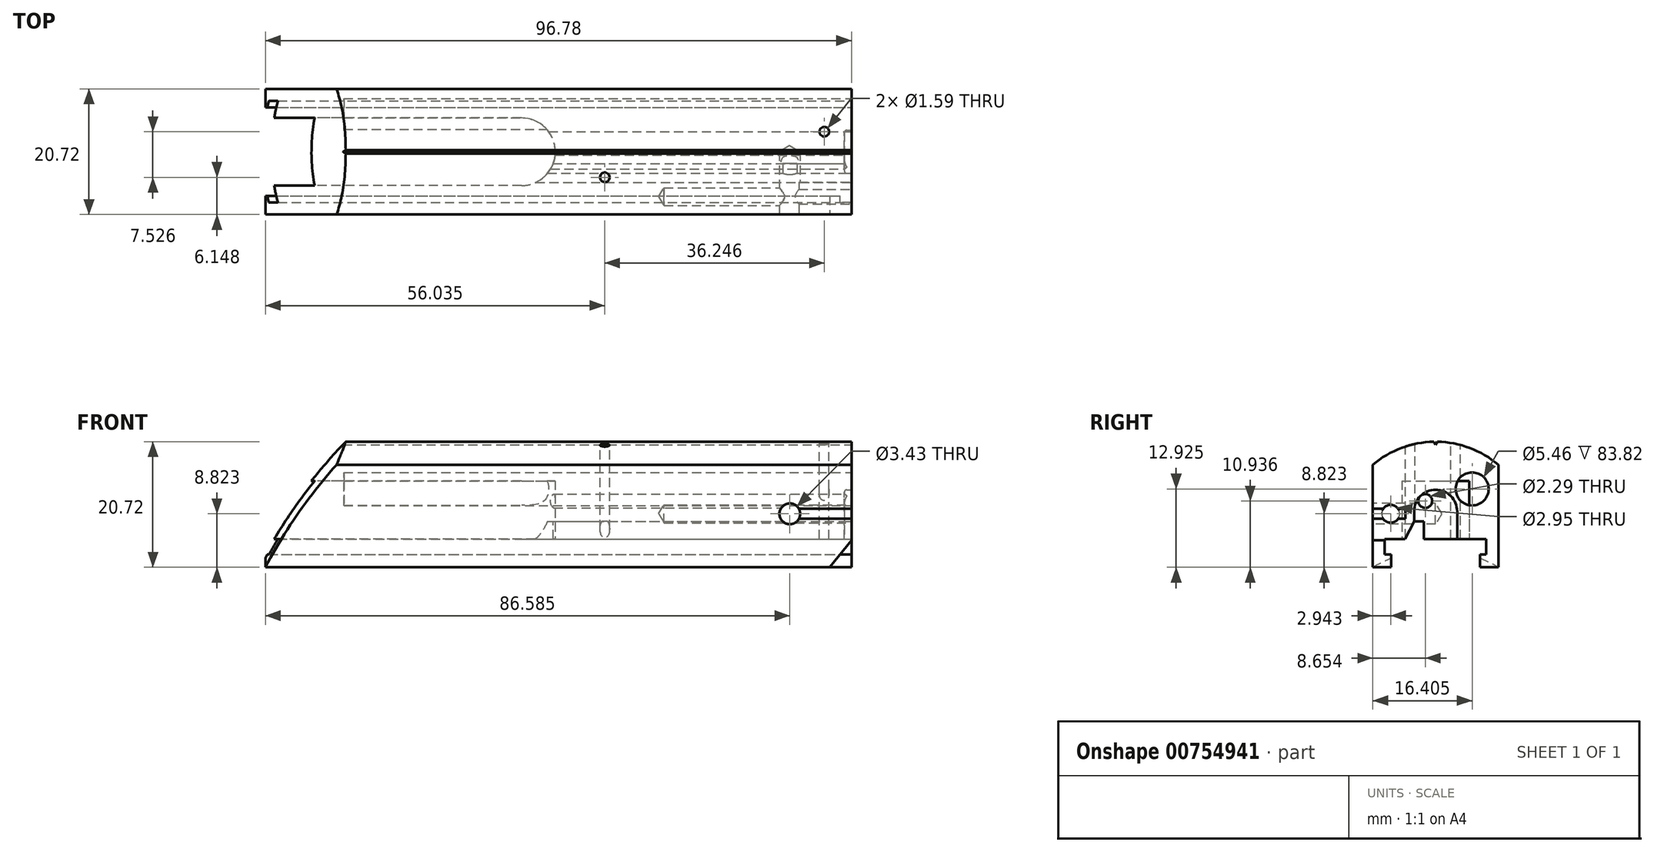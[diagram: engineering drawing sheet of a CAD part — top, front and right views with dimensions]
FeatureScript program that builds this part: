
annotation { "Feature Type Name" : "Feature", "Feature Type Description" : "" }
export const myFeature = defineFeature(function(context is Context, id is Id, definition is map)
    precondition{}
    {
        {
            var Q0;
            Q0=qCreatedBy(makeId("Right.planeOp"),FACE);
            var sketch = newSketch(context, id + "F0", { "sketchPlane" : qUnion([Q0])});
            skLineSegment(sketch, "E0.bottom", {"start": v(-10.36, -10.36) * mm, "end": v(10.36, -10.36) * mm});
            skLineSegment(sketch, "E0.top", {"start": v(-10.36, 10.36) * mm, "end": v(10.36, 10.36) * mm});
            skLineSegment(sketch, "E0.left", {"start": v(-10.36, -10.36) * mm, "end": v(-10.36, 10.36) * mm});
            skLineSegment(sketch, "E0.right", {"start": v(10.36, -10.36) * mm, "end": v(10.36, 10.36) * mm});
            skPoint(sketch, "E0.middle", {"position": v(0, 0) * mm});
            skSolve(sketch);
        }
        {
            var Q0;
            Q0 = qSketchRegion(id + "F0", true);
            var Q1;
            Q1=makeQuery(id+"F0.imprint","IMPRINT",FACE,{"disambiguationData":[TD([[makeQuery(id+"F0.imprint","IMPRINT",EDGE,{"derivedFrom":sQuery(id+"F0.wireOp",EDGE,"E0.bottom")}),1.0]])]});
            extrude(context, id + "F1", {"entities" : qUnion([Q0, Q1]), "endBound" : BoundingType.SYMMETRIC, "depth" : 96.77 * mm, "offsetDistance" : 25.4 * mm});
        }
        {
            var Q0;
            Q0=makeQuery(id+"F1.opExtrude","CAP_FACE",FACE,{"disambiguationData":[OSD([sQuery(id+"F0.wireOp",EDGE,"E0.bottom"),sQuery(id+"F0.wireOp",EDGE,"E0.top"),sQuery(id+"F0.wireOp",EDGE,"E0.left"),sQuery(id+"F0.wireOp",EDGE,"E0.right")])],"isStart":true});
            var sketch = newSketch(context, id + "F2", { "sketchPlane" : qUnion([Q0])});
            skLineSegment(sketch, "E1.bottom", {"start": v(5.58, 3.91) * mm, "end": v(-5.58, 3.91) * mm});
            skLineSegment(sketch, "E1.top", {"start": v(5.58, -10.36) * mm, "end": v(-5.58, -10.36) * mm});
            skLineSegment(sketch, "E1.left", {"start": v(5.58, 3.91) * mm, "end": v(5.58, -10.36) * mm});
            skLineSegment(sketch, "E1.right", {"start": v(-5.58, 3.91) * mm, "end": v(-5.58, -10.36) * mm});
            skSolve(sketch);
        }
        {
            var Q0;
            Q0=makeQuery(id+"F2.imprint","IMPRINT",FACE,{"disambiguationData":[TD([[makeQuery(id+"F2.imprint","IMPRINT",EDGE,{"derivedFrom":sQuery(id+"F2.wireOp",EDGE,"E1.bottom")}),1.0]])]});
            extrude(context, id + "F3", {"entities" : qUnion([Q0]), "operationType" : NewBodyOperationType.REMOVE, "oppositeDirection" : true, "depth" : 47.85 * mm, "offsetDistance" : 25.4 * mm});
        }
        {
            var Q0;
            Q0=makeQuery(id+"F3.boolean.opBoolean","COPY",EDGE,{"derivedFrom":makeQuery(id+"F3.opExtrude","CAP_EDGE",EDGE,{"disambiguationData":[OSD([sQuery(id+"F2.wireOp",EDGE,"E1.right")])],"isStart":false})});
            var Q1;
            Q1=makeQuery(id+"F3.boolean.opBoolean","COPY",EDGE,{"derivedFrom":makeQuery(id+"F3.opExtrude","CAP_EDGE",EDGE,{"disambiguationData":[OSD([sQuery(id+"F2.wireOp",EDGE,"E1.left")])],"isStart":false})});
            fillet(context, id + "F4", {"entities" : qUnion([Q0, Q1]), "radius" : 5.56 * mm, "tangentPropagation" : true, "allowEdgeOverflow" : false});
        }
        {
            var Q0;
            Q0=makeQuery(id+"F1.opExtrude","CAP_FACE",FACE,{"disambiguationData":[OSD([sQuery(id+"F0.wireOp",EDGE,"E0.bottom"),sQuery(id+"F0.wireOp",EDGE,"E0.top"),sQuery(id+"F0.wireOp",EDGE,"E0.left"),sQuery(id+"F0.wireOp",EDGE,"E0.right")])],"isStart":false});
            var sketch = newSketch(context, id + "F5", { "sketchPlane" : qUnion([Q0])});
            skLineSegment(sketch, "E2.bottom", {"start": v(-8.38, -5.7) * mm, "end": v(8.38, -5.7) * mm});
            skLineSegment(sketch, "E2.top", {"start": v(-8.38, -8.26) * mm, "end": v(-7.32, -8.26) * mm});
            skLineSegment(sketch, "E2.left", {"start": v(-8.38, -5.7) * mm, "end": v(-8.38, -8.25) * mm});
            skLineSegment(sketch, "E2.right", {"start": v(8.38, -5.7) * mm, "end": v(8.38, -8.25) * mm});
            skLineSegment(sketch, "E3.top", {"start": v(-7.32, -10.36) * mm, "end": v(7.32, -10.36) * mm});
            skLineSegment(sketch, "E3.left", {"start": v(-7.32, -8.25) * mm, "end": v(-7.32, -10.36) * mm});
            skLineSegment(sketch, "E3.right", {"start": v(7.32, -8.25) * mm, "end": v(7.32, -10.36) * mm});
            skLineSegment(sketch, "E4.trimOffspring", {"start": v(7.32, -8.26) * mm, "end": v(8.38, -8.26) * mm});
            skPoint(sketch, "E5", {"position": v(0, -5.7) * mm});
            skSolve(sketch);
        }
        {
            var Q0;
            Q0=makeQuery(id+"F5.imprint","IMPRINT",FACE,{"disambiguationData":[TD([[makeQuery(id+"F5.imprint","IMPRINT",EDGE,{"derivedFrom":sQuery(id+"F5.wireOp",EDGE,"E2.bottom")}),-1.0]])]});
            extrude(context, id + "F6", {"entities" : qUnion([Q0]), "operationType" : NewBodyOperationType.REMOVE, "endBound" : BoundingType.THROUGH_ALL, "oppositeDirection" : true, "depth" : 25.4 * mm, "offsetDistance" : 25.4 * mm});
        }
        {
            var Q0;
            Q0=makeQuery(id+"F1.opExtrude","CAP_FACE",FACE,{"disambiguationData":[OSD([sQuery(id+"F0.wireOp",EDGE,"E0.bottom"),sQuery(id+"F0.wireOp",EDGE,"E0.top"),sQuery(id+"F0.wireOp",EDGE,"E0.left"),sQuery(id+"F0.wireOp",EDGE,"E0.right")])],"isStart":false});
            var sketch = newSketch(context, id + "F7", { "sketchPlane" : qUnion([Q0])});
            skLineSegment(sketch, "E6.bottom", {"start": v(-1.97, -5.7) * mm, "end": v(-5.08, -5.7) * mm});
            skLineSegment(sketch, "E6.top", {"start": v(-1.97, -2.78) * mm, "end": v(-3.56, -2.78) * mm});
            skLineSegment(sketch, "E6.left", {"start": v(-1.97, -5.7) * mm, "end": v(-1.97, -2.78) * mm});
            skLineSegment(sketch, "E7", {"start": v(-5.08, -5.7) * mm, "end": v(-3.56, -2.78) * mm});
            skPoint(sketch, "E6.right.end.orphan", {"position": v(-5.14, -2.78) * mm});
            skSolve(sketch);
        }
        {
            var Q0;
            Q0=makeQuery(id+"F7.imprint","IMPRINT",FACE,{"disambiguationData":[TD([[makeQuery(id+"F7.imprint","IMPRINT",EDGE,{"derivedFrom":sQuery(id+"F7.wireOp",EDGE,"E6.bottom")}),1.0]])]});
            extrude(context, id + "F8", {"entities" : qUnion([Q0]), "operationType" : NewBodyOperationType.REMOVE, "endBound" : BoundingType.THROUGH_ALL, "oppositeDirection" : true, "depth" : 25.4 * mm, "offsetDistance" : 25.4 * mm});
        }
        {
            var Q0;
            Q0=makeQuery(id+"F1.opExtrude","CAP_FACE",FACE,{"disambiguationData":[OSD([sQuery(id+"F0.wireOp",EDGE,"E0.bottom"),sQuery(id+"F0.wireOp",EDGE,"E0.top"),sQuery(id+"F0.wireOp",EDGE,"E0.left"),sQuery(id+"F0.wireOp",EDGE,"E0.right")])],"isStart":false});
            var sketch = newSketch(context, id + "F9", { "sketchPlane" : qUnion([Q0])});
            skArc(sketch, "E8", {"start": v(3.56, -1.13) * mm, "mid": v(0, 2.43) * mm, "end": v(-3.56, -1.13) * mm});
            skLineSegment(sketch, "E9.top", {"start": v(-3.56, -5.7) * mm, "end": v(3.56, -5.7) * mm});
            skLineSegment(sketch, "E9.left", {"start": v(-3.56, -1.07) * mm, "end": v(-3.56, -5.7) * mm});
            skLineSegment(sketch, "E9.right", {"start": v(3.56, -1.07) * mm, "end": v(3.56, -5.7) * mm});
            skSolve(sketch);
        }
        {
            var Q0;
            {var subQ1=sQuery(id+"F9.wireOp",EDGE,"E8");Q0=makeQuery(id+"F9.imprint","IMPRINT",FACE,{"disambiguationData":[TD([[makeQuery(id+"F9.imprint","IMPRINT",EDGE,{"derivedFrom":subQ1}),1.0]])]});}
            extrude(context, id + "F10", {"entities" : qUnion([Q0]), "operationType" : NewBodyOperationType.REMOVE, "oppositeDirection" : true, "depth" : 1.17 * mm, "offsetDistance" : 25.4 * mm});
        }
        {
            var Q0;
            Q0=makeQuery(id+"F10.boolean.opBoolean","COPY",EDGE,{"derivedFrom":makeQuery(id+"F10.opExtrude","CAP_EDGE",EDGE,{"disambiguationData":[OSD([sQuery(id+"F9.wireOp",EDGE,"E9.right")])],"isStart":false})});
            var Q1;
            Q1=makeQuery(id+"F10.boolean.opBoolean","COPY",EDGE,{"derivedFrom":makeQuery(id+"F10.opExtrude","CAP_EDGE",EDGE,{"disambiguationData":[OSD([sQuery(id+"F9.wireOp",EDGE,"E8")])],"isStart":false})});
            var Q2;
            Q2=makeQuery(id+"F10.boolean.opBoolean","COPY",EDGE,{"derivedFrom":makeQuery(id+"F10.opExtrude","CAP_EDGE",EDGE,{"disambiguationData":[OSD([sQuery(id+"F9.wireOp",EDGE,"E9.left")])],"isStart":false})});
            fillet(context, id + "F11", {"entities" : qUnion([Q0, Q1, Q2]), "radius" : 0.38 * mm, "tangentPropagation" : true, "allowEdgeOverflow" : false});
        }
        {
            var Q0;
            Q0=makeQuery(id+"F1.opExtrude","CAP_FACE",FACE,{"disambiguationData":[OSD([sQuery(id+"F0.wireOp",EDGE,"E0.bottom"),sQuery(id+"F0.wireOp",EDGE,"E0.top"),sQuery(id+"F0.wireOp",EDGE,"E0.left"),sQuery(id+"F0.wireOp",EDGE,"E0.right")])],"isStart":false});
            var sketch = newSketch(context, id + "F12", { "sketchPlane" : qUnion([Q0])});
            skLineSegment(sketch, "E10", {"start": v(-2.51, 1.38) * mm, "end": v(0, -1.13) * mm, "construction": true});
            skPoint(sketch, "E11", {"position": v(-1.7, 0.58) * mm});
            skSolve(sketch);
        }
        {
            var Q0;
            Q0=sQuery(id+"F12.wireOp",VERTEX,"E11");
            var Q1;
            Q1=makeQuery(id+"F1.opExtrude","SWEPT_BODY",BODY,{"disambiguationData":[OSD([sQuery(id+"F0.wireOp",EDGE,"E0.bottom"),sQuery(id+"F0.wireOp",EDGE,"E0.top"),sQuery(id+"F0.wireOp",EDGE,"E0.left"),sQuery(id+"F0.wireOp",EDGE,"E0.right")])]});
            hole(context, id + "F13", {"style" : HoleStyle.SIMPLE, "endStyle" : HoleEndStyle.THROUGH, "holeDiameter" : 2.3 * mm, "majorDiameter" : 6.35 * mm, "isTappedThrough" : true, "tappedDepth" : 18.41 * mm, "tapClearance" : 3, "startFromSketch" : true, "locations" : qUnion([Q0]), "scope" : qUnion([Q1])});
        }
        {
            var Q0;
            Q0=makeQuery(id+"F1.opExtrude","SWEPT_FACE",FACE,{"disambiguationData":[OSD([sQuery(id+"F0.wireOp",EDGE,"E0.left")])]});
            var sketch = newSketch(context, id + "F14", { "sketchPlane" : qUnion([Q0])});
            skPoint(sketch, "E12", {"position": v(38.2, -1.54) * mm});
            skSolve(sketch);
        }
        {
            var Q0;
            Q0=sQuery(id+"F14.wireOp",VERTEX,"E12");
            var Q1;
            Q1=makeQuery(id+"F1.opExtrude","SWEPT_BODY",BODY,{"disambiguationData":[OSD([sQuery(id+"F0.wireOp",EDGE,"E0.bottom"),sQuery(id+"F0.wireOp",EDGE,"E0.top"),sQuery(id+"F0.wireOp",EDGE,"E0.left"),sQuery(id+"F0.wireOp",EDGE,"E0.right")])]});
            hole(context, id + "F15", {"style" : HoleStyle.SIMPLE, "endStyle" : HoleEndStyle.BLIND, "holeDiameter" : 3.43 * mm, "majorDiameter" : 6.35 * mm, "holeDepth" : 10.36 * mm, "isTappedThrough" : true, "tappedDepth" : 18.41 * mm, "tapClearance" : 3, "startFromSketch" : true, "locations" : qUnion([Q0]), "scope" : qUnion([Q1])});
        }
        {
            var Q0;
            Q0=makeQuery(id+"F1.opExtrude","CAP_FACE",FACE,{"disambiguationData":[OSD([sQuery(id+"F0.wireOp",EDGE,"E0.bottom"),sQuery(id+"F0.wireOp",EDGE,"E0.top"),sQuery(id+"F0.wireOp",EDGE,"E0.left"),sQuery(id+"F0.wireOp",EDGE,"E0.right")])],"isStart":false});
            var sketch = newSketch(context, id + "F16", { "sketchPlane" : qUnion([Q0])});
            skPoint(sketch, "E13", {"position": v(-7.42, -1.54) * mm});
            skSolve(sketch);
        }
        {
            var Q0;
            Q0=sQuery(id+"F16.wireOp",VERTEX,"E13");
            var Q1;
            Q1=makeQuery(id+"F1.opExtrude","SWEPT_BODY",BODY,{"disambiguationData":[OSD([sQuery(id+"F0.wireOp",EDGE,"E0.bottom"),sQuery(id+"F0.wireOp",EDGE,"E0.top"),sQuery(id+"F0.wireOp",EDGE,"E0.left"),sQuery(id+"F0.wireOp",EDGE,"E0.right")])]});
            hole(context, id + "F17", {"style" : HoleStyle.SIMPLE, "endStyle" : HoleEndStyle.BLIND, "holeDiameter" : 2.95 * mm, "majorDiameter" : 6.35 * mm, "holeDepth" : 30.96 * mm, "isTappedThrough" : true, "tappedDepth" : 18.41 * mm, "tapClearance" : 3, "startFromSketch" : true, "locations" : qUnion([Q0]), "scope" : qUnion([Q1])});
        }
        {
            var Q0;
            Q0=makeQuery(id+"F1.opExtrude","SWEPT_FACE",FACE,{"disambiguationData":[OSD([sQuery(id+"F0.wireOp",EDGE,"E0.left")])]});
            var sketch = newSketch(context, id + "F18", { "sketchPlane" : qUnion([Q0])});
            skLineSegment(sketch, "E14.bottom", {"start": v(38.2, -0.7) * mm, "end": v(48.39, -0.7) * mm});
            skLineSegment(sketch, "E14.top", {"start": v(38.2, -2.37) * mm, "end": v(48.39, -2.37) * mm});
            skLineSegment(sketch, "E14.left", {"start": v(38.2, -0.7) * mm, "end": v(38.2, -2.37) * mm});
            skLineSegment(sketch, "E14.right", {"start": v(48.39, -0.7) * mm, "end": v(48.39, -2.37) * mm});
            skPoint(sketch, "E15", {"position": v(38.2, -1.54) * mm});
            skSolve(sketch);
        }
        {
            var Q0;
            {var subQ0=sQuery(id+"F18.wireOp",EDGE,"E14.left");Q0=makeQuery(id+"F18.imprint","IMPRINT",FACE,{"disambiguationData":[TD([[makeQuery(id+"F18.imprint","IMPRINT",EDGE,{"derivedFrom":subQ0}),1.0]])]});}
            var Q1;
            {var subQ0=sQuery(id+"F18.wireOp",EDGE,"E14.right");Q1=makeQuery(id+"F18.imprint","IMPRINT",FACE,{"disambiguationData":[TD([[makeQuery(id+"F18.imprint","IMPRINT",EDGE,{"derivedFrom":subQ0}),1.0]])]});}
            extrude(context, id + "F19", {"entities" : qUnion([Q0, Q1]), "operationType" : NewBodyOperationType.REMOVE, "oppositeDirection" : true, "depth" : 5.36 * mm, "offsetDistance" : 25.4 * mm});
        }
        {
            var Q0;
            Q0=makeQuery(id+"F1.opExtrude","CAP_FACE",FACE,{"disambiguationData":[OSD([sQuery(id+"F0.wireOp",EDGE,"E0.bottom"),sQuery(id+"F0.wireOp",EDGE,"E0.top"),sQuery(id+"F0.wireOp",EDGE,"E0.left"),sQuery(id+"F0.wireOp",EDGE,"E0.right")])],"isStart":false});
            var sketch = newSketch(context, id + "F20", { "sketchPlane" : qUnion([Q0])});
            skPoint(sketch, "E16", {"position": v(6.05, 2.57) * mm});
            skCircle(sketch, "E17", {"center": v(6.05, 2.57) * mm, "radius": 2.73 * mm});
            skSolve(sketch);
        }
        {
            var Q0;
            Q0=makeQuery(id+"F20.imprint","IMPRINT",FACE,{"disambiguationData":[TD([[makeQuery(id+"F20.imprint","IMPRINT",EDGE,{"derivedFrom":sQuery(id+"F20.wireOp",EDGE,"E17")}),1.0]])]});
            extrude(context, id + "F21", {"entities" : qUnion([Q0]), "operationType" : NewBodyOperationType.REMOVE, "oppositeDirection" : true, "depth" : 83.82 * mm, "offsetDistance" : 25.4 * mm});
        }
        {
            var Q0;
            Q0=makeQuery(id+"F1.opExtrude","SWEPT_FACE",FACE,{"disambiguationData":[OSD([sQuery(id+"F0.wireOp",EDGE,"E0.top")])]});
            var sketch = newSketch(context, id + "F22", { "sketchPlane" : qUnion([Q0])});
            skPoint(sketch, "E18", {"position": v(43.9, 3.31) * mm});
            skSolve(sketch);
        }
        {
            var Q0;
            Q0=sQuery(id+"F22.wireOp",VERTEX,"E18");
            var Q1;
            Q1=makeQuery(id+"F1.opExtrude","SWEPT_BODY",BODY,{"disambiguationData":[OSD([sQuery(id+"F0.wireOp",EDGE,"E0.bottom"),sQuery(id+"F0.wireOp",EDGE,"E0.top"),sQuery(id+"F0.wireOp",EDGE,"E0.left"),sQuery(id+"F0.wireOp",EDGE,"E0.right")])]});
            hole(context, id + "F23", {"style" : HoleStyle.SIMPLE, "endStyle" : HoleEndStyle.THROUGH, "holeDiameter" : 1.59 * mm, "majorDiameter" : 6.35 * mm, "isTappedThrough" : true, "tappedDepth" : 18.41 * mm, "tapClearance" : 3, "startFromSketch" : true, "locations" : qUnion([Q0]), "scope" : qUnion([Q1])});
        }
        {
            var Q0;
            Q0=makeQuery(id+"F1.opExtrude","SWEPT_FACE",FACE,{"disambiguationData":[OSD([sQuery(id+"F0.wireOp",EDGE,"E0.top")])]});
            var sketch = newSketch(context, id + "F24", { "sketchPlane" : qUnion([Q0])});
            skPoint(sketch, "E19", {"position": v(7.65, -4.21) * mm});
            skSolve(sketch);
        }
        {
            var Q0;
            Q0=sQuery(id+"F24.wireOp",VERTEX,"E19");
            var Q1;
            Q1=makeQuery(id+"F1.opExtrude","SWEPT_BODY",BODY,{"disambiguationData":[OSD([sQuery(id+"F0.wireOp",EDGE,"E0.bottom"),sQuery(id+"F0.wireOp",EDGE,"E0.top"),sQuery(id+"F0.wireOp",EDGE,"E0.left"),sQuery(id+"F0.wireOp",EDGE,"E0.right")])]});
            hole(context, id + "F25", {"style" : HoleStyle.SIMPLE, "endStyle" : HoleEndStyle.THROUGH, "holeDiameter" : 1.59 * mm, "majorDiameter" : 6.35 * mm, "isTappedThrough" : true, "tappedDepth" : 18.41 * mm, "tapClearance" : 3, "startFromSketch" : true, "locations" : qUnion([Q0]), "scope" : qUnion([Q1])});
        }
        {
            var Q0;
            Q0=makeQuery(id+"F1.opExtrude","SWEPT_FACE",FACE,{"disambiguationData":[OSD([sQuery(id+"F0.wireOp",EDGE,"E0.left")])]});
            var sketch = newSketch(context, id + "F26", { "sketchPlane" : qUnion([Q0])});
            skLineSegment(sketch, "E20", {"start": v(44.82, -10.36) * mm, "end": v(48.39, -10.36) * mm});
            skLineSegment(sketch, "E21", {"start": v(48.39, -10.36) * mm, "end": v(48.39, -5.92) * mm});
            skLineSegment(sketch, "E22", {"start": v(48.39, -5.92) * mm, "end": v(44.82, -10.36) * mm});
            skSolve(sketch);
        }
        {
            var Q0;
            Q0=makeQuery(id+"F26.imprint","IMPRINT",FACE,{"disambiguationData":[TD([[makeQuery(id+"F26.imprint","IMPRINT",EDGE,{"derivedFrom":sQuery(id+"F26.wireOp",EDGE,"E20")}),-1.0]])]});
            var Q1;
            {var subQ0=sQuery(id+"F0.wireOp",EDGE,"E0.bottom");Q1=makeQuery(id+"F6.boolean.opBoolean","COPY",FACE,{"disambiguationData":[TD([makeQuery(id+"F1.opExtrude","CAP_FACE",FACE,{"disambiguationData":[OSD([subQ0,sQuery(id+"F0.wireOp",EDGE,"E0.top"),sQuery(id+"F0.wireOp",EDGE,"E0.left"),sQuery(id+"F0.wireOp",EDGE,"E0.right")])],"isStart":false})])],"derivedFrom":makeQuery(id+"F6.opExtrude","SWEPT_FACE",FACE,{"disambiguationData":[OSD([sQuery(id+"F5.wireOp",EDGE,"E3.left")])]})});}
            extrude(context, id + "F27", {"entities" : qUnion([Q0]), "operationType" : NewBodyOperationType.REMOVE, "endBound" : BoundingType.UP_TO_SURFACE, "oppositeDirection" : true, "depth" : 25.4 * mm, "endBoundEntityFace" : qUnion([Q1]), "offsetDistance" : 25.4 * mm});
        }
        {
            var Q0;
            {var subQ0=sQuery(id+"F0.wireOp",EDGE,"E0.bottom");var subQ1=sQuery(id+"F0.wireOp",EDGE,"E0.left");Q0=makeQuery(id+"F3.boolean.opBoolean","SPLIT",EDGE,{"disambiguationData":[TD([makeQuery(id+"F1.opExtrude","SWEPT_FACE",FACE,{"disambiguationData":[OSD([subQ1])]})])],"derivedFrom":makeQuery(id+"F1.opExtrude","CAP_EDGE",EDGE,{"disambiguationData":[OSD([subQ0])],"isStart":true})});}
            var Q1;
            Q1=makeQuery(id+"F1.opExtrude","CAP_FACE",FACE,{"disambiguationData":[OSD([sQuery(id+"F0.wireOp",EDGE,"E0.bottom"),sQuery(id+"F0.wireOp",EDGE,"E0.top"),sQuery(id+"F0.wireOp",EDGE,"E0.left"),sQuery(id+"F0.wireOp",EDGE,"E0.right")])],"isStart":true});
            cPlane(context, id + "F28", {"entities" : qUnion([Q0, Q1]), "cplaneType" : CPlaneType.LINE_ANGLE, "offset" : 25.4 * mm, "angle" : 60 * degree, "oppositeDirection" : true, "width" : 152.4 * mm, "height" : 152.4 * mm});
        }
        {
            var Q0;
            Q0=qCreatedBy(id+"F28.planeOp",FACE);
            var sketch = newSketch(context, id + "F29", { "sketchPlane" : qUnion([Q0])});
            skArc(sketch, "E23", {"start": v(-0.06, 38.1) * mm, "mid": v(-38.16, 0) * mm, "end": v(-0.06, -38.1) * mm});
            skLineSegment(sketch, "E24", {"start": v(-0.06, -38.1) * mm, "end": v(-0.06, 38.1) * mm, "construction": true});
            skSolve(sketch);
        }
        {
            var Q0;
            Q0=qCreatedBy(id+"F28.planeOp",FACE);
            var Q1;
            Q1=sQuery(id+"F29.wireOp",EDGE,"E24");
            cPlane(context, id + "F30", {"entities" : qUnion([Q0, Q1]), "cplaneType" : CPlaneType.LINE_ANGLE, "offset" : 25.4 * mm, "angle" : 90 * degree, "oppositeDirection" : true, "width" : 152.4 * mm, "height" : 152.4 * mm});
        }
        {
            var Q0;
            Q0=qCreatedBy(id+"F30.planeOp",FACE);
            var sketch = newSketch(context, id + "F31", { "sketchPlane" : qUnion([Q0])});
            skArc(sketch, "E25", {"start": v(-24.13, 17.63) * mm, "mid": v(-35.04, -6.69) * mm, "end": v(-38.1, -33.17) * mm});
            skLineSegment(sketch, "E26", {"start": v(-24.13, 17.63) * mm, "end": v(-101.54, 17.63) * mm});
            skLineSegment(sketch, "E27", {"start": v(-101.54, 17.63) * mm, "end": v(-101.54, -33.17) * mm});
            skLineSegment(sketch, "E28", {"start": v(-101.54, -33.17) * mm, "end": v(-38.1, -33.17) * mm});
            skSolve(sketch);
        }
        {
            var Q0;
            Q0=makeQuery(id+"F31.imprint","IMPRINT",FACE,{"disambiguationData":[TD([[makeQuery(id+"F31.imprint","IMPRINT",EDGE,{"derivedFrom":sQuery(id+"F31.wireOp",EDGE,"E25")}),-1.0]])]});
            var Q1;
            Q1=sQuery(id+"F29.wireOp",EDGE,"E23");
            sweep(context, id + "F32", {"operationType" : NewBodyOperationType.REMOVE, "profiles" : qUnion([Q0]), "path" : qUnion([Q1])});
        }
        {
            var Q0;
            Q0=makeQuery(id+"F1.opExtrude","CAP_FACE",FACE,{"disambiguationData":[OSD([sQuery(id+"F0.wireOp",EDGE,"E0.bottom"),sQuery(id+"F0.wireOp",EDGE,"E0.top"),sQuery(id+"F0.wireOp",EDGE,"E0.left"),sQuery(id+"F0.wireOp",EDGE,"E0.right")])],"isStart":false});
            var sketch = newSketch(context, id + "F33", { "sketchPlane" : qUnion([Q0])});
            skArc(sketch, "E29", {"start": v(10.36, 6.55) * mm, "mid": v(0, 10.36) * mm, "end": v(-10.36, 6.55) * mm});
            skLineSegment(sketch, "E30.0", {"start": v(-10.36, -0.7) * mm, "end": v(-10.36, 10.36) * mm});
            skLineSegment(sketch, "E31.0", {"start": v(10.36, -10.36) * mm, "end": v(10.36, 10.36) * mm});
            skLineSegment(sketch, "E32", {"start": v(-10.36, 6.55) * mm, "end": v(-10.36, 13.54) * mm});
            skLineSegment(sketch, "E33", {"start": v(-10.36, 13.54) * mm, "end": v(10.36, 13.54) * mm});
            skLineSegment(sketch, "E34", {"start": v(10.36, 13.54) * mm, "end": v(10.36, 6.55) * mm});
            skSolve(sketch);
        }
        {
            var Q0;
            {var subQ0=sQuery(id+"F33.wireOp",EDGE,"E32");var subQ3=makeQuery(id+"F1.opExtrude","CAP_EDGE",EDGE,{"disambiguationData":[OSD([sQuery(id+"F0.wireOp",EDGE,"E0.top")])],"isStart":false});var subQ5=makeQuery(id+"F33.imprint","INTERSECT",VERTEX,{"derivedFrom":[subQ3,subQ0]});Q0=makeQuery(id+"F33.imprint","IMPRINT",FACE,{"disambiguationData":[TD([[makeQuery(id+"F33.imprint","IMPRINT",EDGE,{"disambiguationData":[TD([[subQ5,-1.0]])],"derivedFrom":subQ3}),-1.0]])]});}
            var Q1;
            {var subQ0=sQuery(id+"F33.wireOp",EDGE,"E34");var subQ3=makeQuery(id+"F1.opExtrude","CAP_EDGE",EDGE,{"disambiguationData":[OSD([sQuery(id+"F0.wireOp",EDGE,"E0.top")])],"isStart":false});var subQ5=makeQuery(id+"F33.imprint","INTERSECT",VERTEX,{"derivedFrom":[subQ3,subQ0]});Q1=makeQuery(id+"F33.imprint","IMPRINT",FACE,{"disambiguationData":[TD([[makeQuery(id+"F33.imprint","IMPRINT",EDGE,{"disambiguationData":[TD([[subQ5,1.0]])],"derivedFrom":subQ3}),-1.0]])]});}
            extrude(context, id + "F34", {"entities" : qUnion([Q0, Q1]), "operationType" : NewBodyOperationType.REMOVE, "endBound" : BoundingType.THROUGH_ALL, "oppositeDirection" : true, "depth" : 25.4 * mm, "offsetDistance" : 25.4 * mm});
        }
        {
            var Q0;
            Q0=makeQuery(id+"F1.opExtrude","CAP_FACE",FACE,{"disambiguationData":[OSD([sQuery(id+"F0.wireOp",EDGE,"E0.bottom"),sQuery(id+"F0.wireOp",EDGE,"E0.top"),sQuery(id+"F0.wireOp",EDGE,"E0.left"),sQuery(id+"F0.wireOp",EDGE,"E0.right")])],"isStart":false});
            var sketch = newSketch(context, id + "F35", { "sketchPlane" : qUnion([Q0])});
            skLineSegment(sketch, "E35", {"start": v(0, 9.88) * mm, "end": v(-0.32, 10.43) * mm});
            skLineSegment(sketch, "E36", {"start": v(-0.32, 10.43) * mm, "end": v(0.32, 10.43) * mm});
            skLineSegment(sketch, "E37", {"start": v(0.32, 10.43) * mm, "end": v(0, 9.88) * mm});
            skPoint(sketch, "E38", {"position": v(0, 10.36) * mm});
            skSolve(sketch);
        }
        {
            var Q0;
            {var subQ0=sQuery(id+"F35.wireOp",EDGE,"E37");var subQ1=sQuery(id+"F35.wireOp",EDGE,"E35");var subQ2=makeQuery(id+"F35.imprint","INTERSECT",VERTEX,{"derivedFrom":[subQ1,subQ0]});Q0=makeQuery(id+"F35.imprint","IMPRINT",FACE,{"disambiguationData":[TD([[makeQuery(id+"F35.imprint","IMPRINT",EDGE,{"disambiguationData":[TD([[subQ2,-1.0]])],"derivedFrom":subQ1}),-1.0]])]});}
            extrude(context, id + "F36", {"entities" : qUnion([Q0]), "operationType" : NewBodyOperationType.REMOVE, "endBound" : BoundingType.THROUGH_ALL, "oppositeDirection" : true, "depth" : 25.4 * mm, "offsetDistance" : 25.4 * mm});
        }
    });
